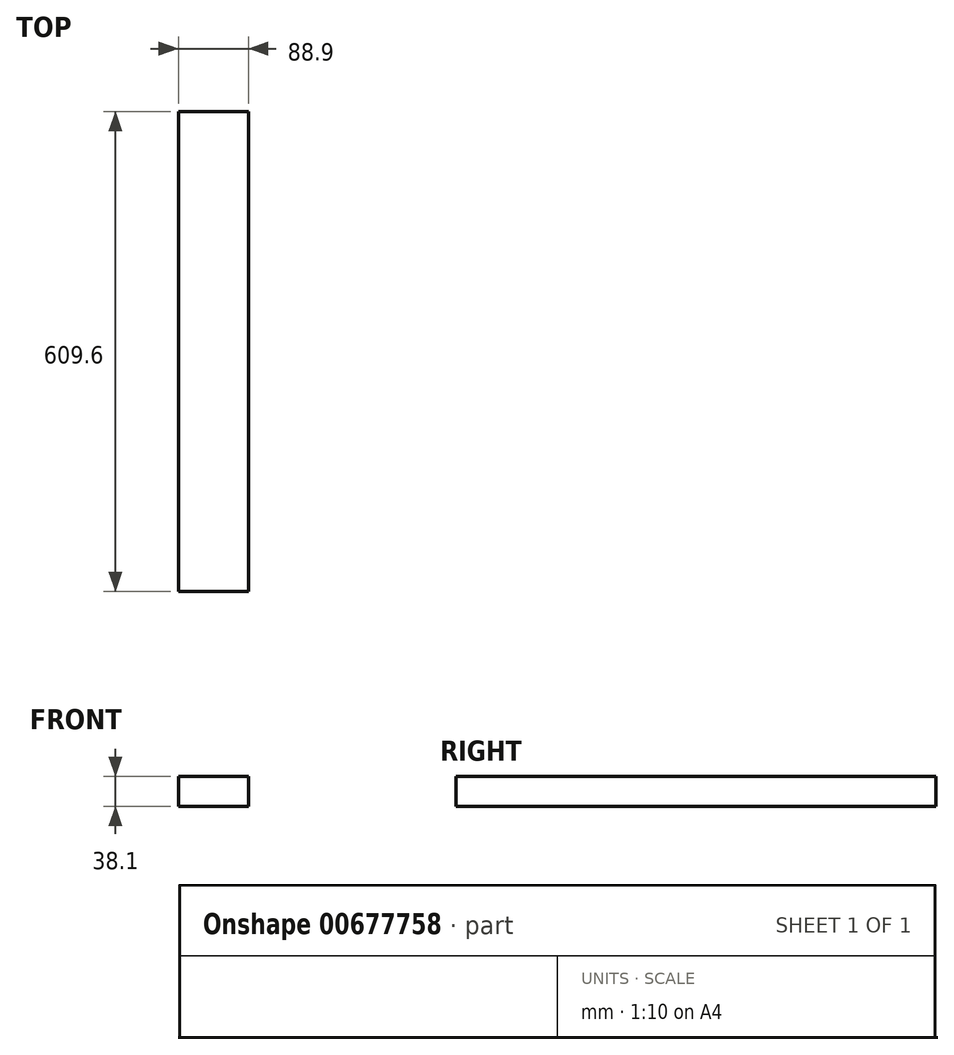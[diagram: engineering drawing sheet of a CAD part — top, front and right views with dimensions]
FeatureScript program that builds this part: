
annotation { "Feature Type Name" : "Feature", "Feature Type Description" : "" }
export const myFeature = defineFeature(function(context is Context, id is Id, definition is map)
    precondition{}
    {
        {
            var Q0;
            Q0=qCreatedBy(makeId("Front.planeOp"),FACE);
            var sketch = newSketch(context, id + "F0", { "sketchPlane" : qUnion([Q0])});
            skLineSegment(sketch, "E0.bottom", {"start": v(1813.14, -272.83) * mm, "end": v(1902.04, -272.83) * mm});
            skLineSegment(sketch, "E0.top", {"start": v(1813.14, -310.93) * mm, "end": v(1902.04, -310.93) * mm});
            skLineSegment(sketch, "E0.left", {"start": v(1813.14, -272.83) * mm, "end": v(1813.14, -310.93) * mm});
            skLineSegment(sketch, "E0.right", {"start": v(1902.04, -272.83) * mm, "end": v(1902.04, -310.93) * mm});
            skSolve(sketch);
        }
        {
            var Q0;
            Q0=makeQuery(id+"F0.imprint","IMPRINT",FACE,{"disambiguationData":[TD([[makeQuery(id+"F0.imprint","IMPRINT",EDGE,{"derivedFrom":sQuery(id+"F0.wireOp",EDGE,"E0.bottom")}),-1.0]])]});
            extrude(context, id + "F1", {"entities" : qUnion([Q0]), "depth" : 609.6 * mm, "offsetDistance" : 25.4 * mm});
        }
    });
